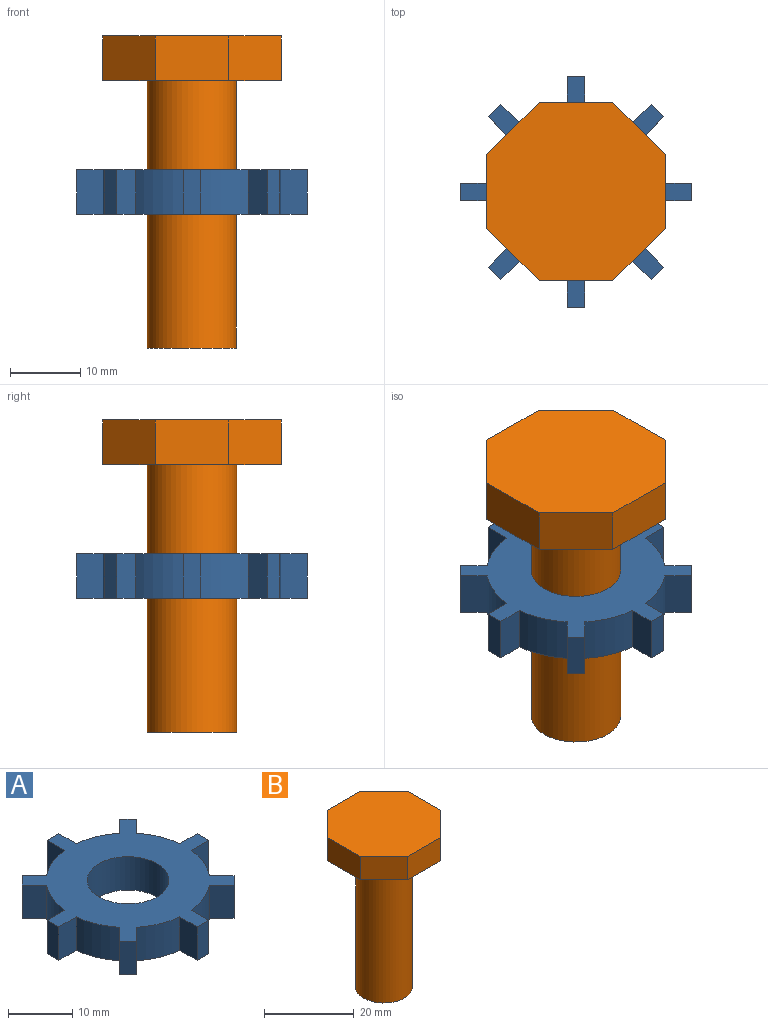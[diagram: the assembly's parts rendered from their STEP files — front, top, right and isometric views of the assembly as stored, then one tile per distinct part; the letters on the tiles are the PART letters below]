
ASSEMBLY  parts=2 mates=1
PART A: 35 faces, bbox 32.9x32.9x6.4 mm
  f0: plane 6.35x2.54mm, normal (-1,0,0), area 16.1mm2, adj f1,f32,f33,f34
  f1: plane 6.35x3.81mm, normal (0,-1,0), area 24.2mm2, adj f0,f2,f33,f34
  f2: cylinder r=12.7mm len=6.77mm, axis (0,0,-1), area 47.2mm2, adj f1,f3,f33,f34
  f3: plane 6.35x2.69mm, normal (-0.71,0.71,0), area 24.2mm2, adj f2,f4,f33,f34
  f4: plane 6.35x1.8mm, normal (-0.71,-0.71,0), area 16.1mm2, adj f3,f5,f33,f34
  f5: plane 6.35x2.69mm, normal (0.71,-0.71,0), area 24.2mm2, adj f4,f6,f33,f34
  f6: cylinder r=12.7mm len=6.77mm, axis (0,0,-1), area 47.2mm2, adj f5,f7,f33,f34
  f7: plane 6.35x3.81mm, normal (-1,0,0), area 24.2mm2, adj f6,f8,f33,f34
  f8: plane 6.35x2.54mm, normal (0,-1,0), area 16.1mm2, adj f7,f9,f33,f34
  f9: plane 6.35x3.81mm, normal (1,0,0), area 24.2mm2, adj f8,f10,f33,f34
  f10: cylinder r=12.7mm len=6.77mm, axis (0,0,-1), area 47.2mm2, adj f9,f11,f33,f34
  f11: plane 6.35x2.69mm, normal (-0.71,-0.71,0), area 24.2mm2, adj f10,f12,f33,f34
  f12: plane 6.35x1.8mm, normal (0.71,-0.71,0), area 16.1mm2, adj f11,f13,f33,f34
  f13: plane 6.35x2.69mm, normal (0.71,0.71,0), area 24.2mm2, adj f12,f14,f33,f34
  f14: cylinder r=12.7mm len=6.77mm, axis (0,0,-1), area 47.2mm2, adj f13,f15,f33,f34
  f15: plane 6.35x3.81mm, normal (0,-1,0), area 24.2mm2, adj f14,f16,f33,f34
  f16: plane 6.35x2.54mm, normal (1,0,0), area 16.1mm2, adj f15,f17,f33,f34
  f17: plane 6.35x3.81mm, normal (0,1,0), area 24.2mm2, adj f16,f18,f33,f34
  f18: cylinder r=12.7mm len=6.77mm, axis (0,0,-1), area 47.2mm2, adj f17,f19,f33,f34
  f19: plane 6.35x2.69mm, normal (0.71,-0.71,0), area 24.2mm2, adj f18,f20,f33,f34
  f20: plane 6.35x1.8mm, normal (0.71,0.71,0), area 16.1mm2, adj f19,f21,f33,f34
  f21: plane 6.35x2.69mm, normal (-0.71,0.71,0), area 24.2mm2, adj f20,f22,f33,f34
  f22: cylinder r=12.7mm len=6.77mm, axis (0,0,-1), area 47.2mm2, adj f21,f23,f33,f34
  f23: plane 6.35x3.81mm, normal (1,0,0), area 24.2mm2, adj f22,f24,f33,f34
  f24: plane 6.35x2.54mm, normal (0,1,0), area 16.1mm2, adj f23,f25,f33,f34
  f25: plane 6.35x3.81mm, normal (-1,0,0), area 24.2mm2, adj f24,f26,f33,f34
  f26: cylinder r=12.7mm len=6.77mm, axis (0,0,-1), area 47.2mm2, adj f25,f27,f33,f34
  f27: plane 6.35x2.69mm, normal (0.71,0.71,0), area 24.2mm2, adj f26,f28,f33,f34
  f28: plane 6.35x1.8mm, normal (-0.71,0.71,0), area 16.1mm2, adj f27,f29,f33,f34
  f29: plane 6.35x2.69mm, normal (-0.71,-0.71,0), area 24.2mm2, adj f28,f30,f33,f34
  f30: cylinder r=12.7mm len=6.77mm, axis (0,0,-1), area 47.2mm2, adj f29,f32,f33,f34
  f31: cylinder r=6.35mm len=12.7mm, axis (0,0,-1), area 253.4mm2, adj f33,f34
  f32: plane 6.35x3.81mm, normal (0,1,0), area 24.2mm2, adj f0,f30,f33,f34
  f33: plane 32.89x32.89mm, normal (0,0,1), area 456.6mm2, adj f0,f1,f2,f3,f4,f5,f6,f7
  f34: plane 32.89x32.89mm, normal (0,0,-1), area 456.6mm2, adj f0,f1,f2,f3,f4,f5,f6,f7
PART B: 12 faces, bbox 25.4x25.4x44.5 mm
  f0: plane 7.44x7.44mm, normal (-0.71,-0.71,0), area 66.8mm2, adj f1,f7,f8,f9
  f1: plane 10.52x6.35mm, normal (0,-1,0), area 66.8mm2, adj f0,f2,f8,f9
  f2: plane 7.44x7.44mm, normal (0.71,-0.71,0), area 66.8mm2, adj f1,f3,f8,f9
  f3: plane 10.52x6.35mm, normal (1,0,0), area 66.8mm2, adj f2,f4,f8,f9
  f4: plane 7.44x7.44mm, normal (0.71,0.71,0), area 66.8mm2, adj f3,f5,f8,f9
  f5: plane 10.52x6.35mm, normal (0,1,0), area 66.8mm2, adj f4,f6,f8,f9
  f6: plane 7.44x7.44mm, normal (-0.71,0.71,0), area 66.8mm2, adj f5,f7,f8,f9
  f7: plane 10.52x6.35mm, normal (-1,0,0), area 66.8mm2, adj f0,f6,f8,f9
  f8: plane 25.4x25.4mm, normal (0,0,1), area 534.5mm2, adj f0,f1,f2,f3,f4,f5,f6,f7
  f9: plane 25.4x25.4mm, normal (0,0,-1), area 407.8mm2, adj f0,f1,f2,f3,f4,f5,f6,f7
  f10: cylinder r=6.35mm len=38.1mm, axis (0,0,1), area 1520.1mm2, adj f9,f11
  f11: plane 12.7x12.7mm, normal (0,0,-1), area 126.7mm2, adj f10
PLACE A t=(0,0,-110.49)mm
PLACE B t=(0,0,-91.44)mm
MATE fastened A.f31 <-> B.f10  axis (0,0,-1) through (0,0,-104.14)mm
